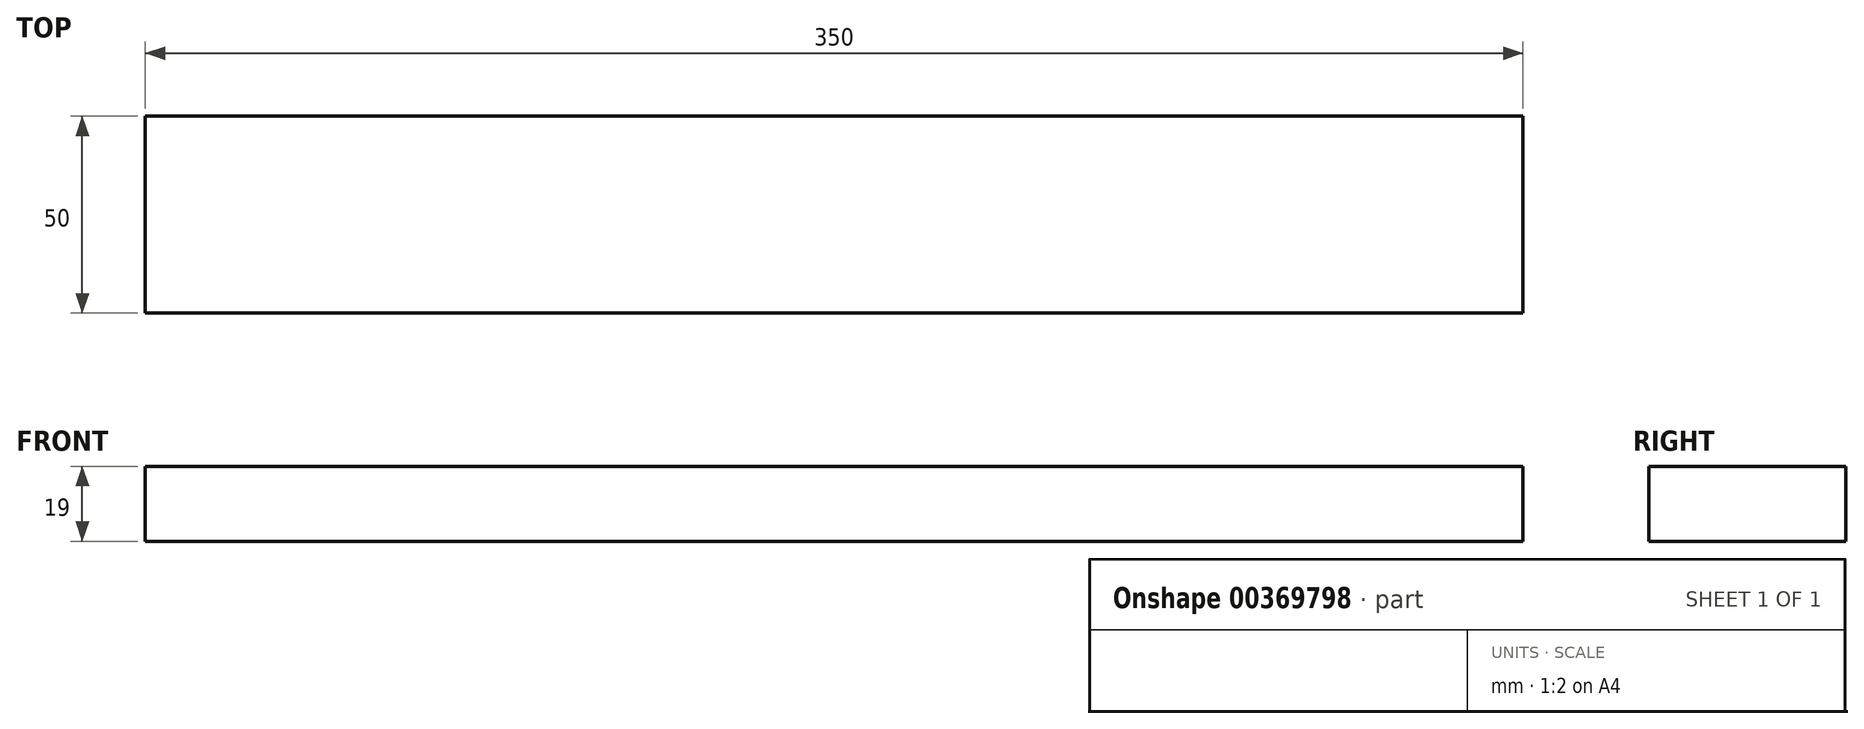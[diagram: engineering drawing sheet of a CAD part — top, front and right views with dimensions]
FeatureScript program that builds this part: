
annotation { "Feature Type Name" : "Feature", "Feature Type Description" : "" }
export const myFeature = defineFeature(function(context is Context, id is Id, definition is map)
    precondition{}
    {
        {
            var Q0;
            Q0=qCreatedBy(makeId("Top.planeOp"),FACE);
            var sketch = newSketch(context, id + "F0", { "sketchPlane" : qUnion([Q0])});
            skLineSegment(sketch, "E0.bottom", {"start": v(0, 0) * mm, "end": v(350, 0) * mm});
            skLineSegment(sketch, "E0.top", {"start": v(0, 50) * mm, "end": v(350, 50) * mm});
            skLineSegment(sketch, "E0.left", {"start": v(0, 0) * mm, "end": v(0, 50) * mm});
            skLineSegment(sketch, "E0.right", {"start": v(350, 0) * mm, "end": v(350, 50) * mm});
            skSolve(sketch);
        }
        {
            var Q0;
            Q0=makeQuery(id+"F0.imprint","IMPRINT",FACE,{"disambiguationData":[TD([[makeQuery(id+"F0.imprint","IMPRINT",EDGE,{"derivedFrom":sQuery(id+"F0.wireOp",EDGE,"E0.bottom")}),1.0]])]});
            extrude(context, id + "F1", {"entities" : qUnion([Q0]), "depth" : 19 * mm});
        }
    });
